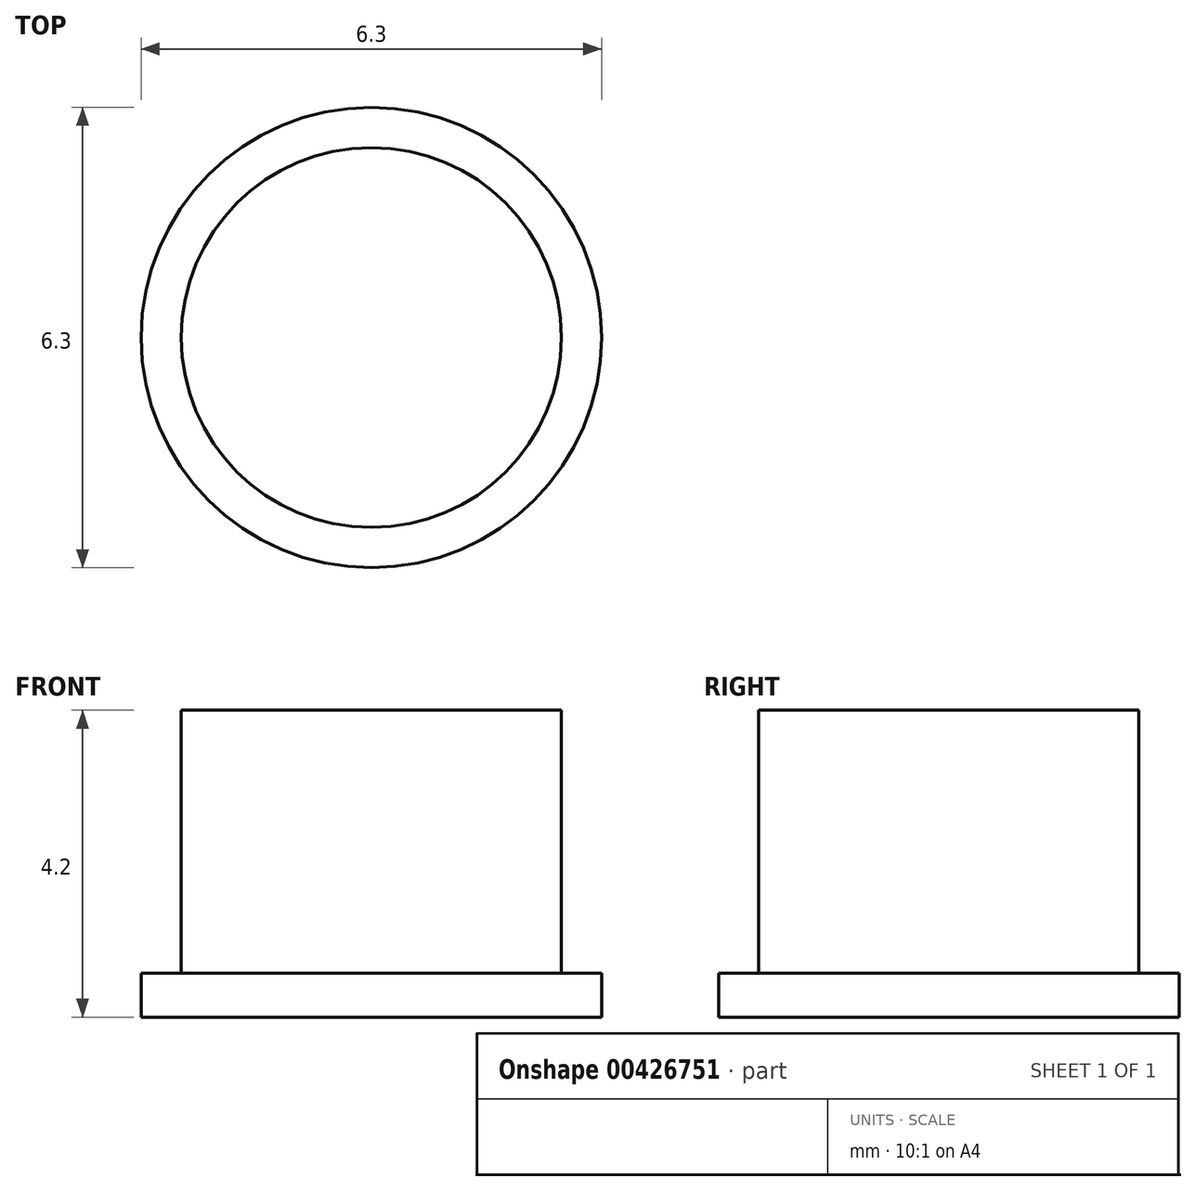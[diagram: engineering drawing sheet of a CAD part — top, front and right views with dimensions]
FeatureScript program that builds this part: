
annotation { "Feature Type Name" : "Feature", "Feature Type Description" : "" }
export const myFeature = defineFeature(function(context is Context, id is Id, definition is map)
    precondition{}
    {
        {
            var Q0;
            Q0=qCreatedBy(makeId("Top.planeOp"),FACE);
            var sketch = newSketch(context, id + "F0", { "sketchPlane" : qUnion([Q0])});
            skCircle(sketch, "E0", {"center": v(0, 0) * mm, "radius": 3.15 * mm});
            skSolve(sketch);
        }
        {
            var Q0;
            Q0=makeQuery(id+"F0.imprint","IMPRINT",FACE,{"disambiguationData":[TD([[makeQuery(id+"F0.imprint","IMPRINT",EDGE,{"derivedFrom":sQuery(id+"F0.wireOp",EDGE,"E0")}),1.0]])]});
            extrude(context, id + "F1", {"entities" : qUnion([Q0]), "depth" : .6 * mm});
        }
        {
            var Q0;
            Q0=makeQuery(id+"F1.opExtrude","CAP_FACE",FACE,{"disambiguationData":[OSD([sQuery(id+"F0.wireOp",EDGE,"E0")])],"isStart":false});
            var sketch = newSketch(context, id + "F2", { "sketchPlane" : qUnion([Q0])});
            skCircle(sketch, "E1", {"center": v(0, 0) * mm, "radius": 2.6 * mm});
            skSolve(sketch);
        }
        {
            var Q0;
            Q0=makeQuery(id+"F2.imprint","IMPRINT",FACE,{"disambiguationData":[TD([[makeQuery(id+"F2.imprint","IMPRINT",EDGE,{"derivedFrom":sQuery(id+"F2.wireOp",EDGE,"E1")}),1.0]])]});
            extrude(context, id + "F3", {"entities" : qUnion([Q0]), "depth" : 3.6 * mm});
        }
    });
